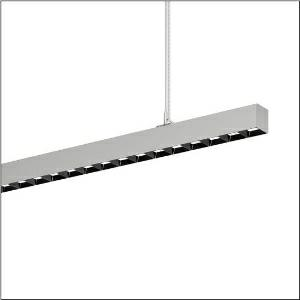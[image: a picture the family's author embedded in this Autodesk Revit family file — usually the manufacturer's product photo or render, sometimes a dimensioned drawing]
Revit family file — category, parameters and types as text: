
# Revit family: silica_r__21_51mx32tctds_853f
name_source: partatom
category: Lighting Fixtures
units: mm (PartAtom-declared; Revit-internal decimal feet)

## family parameters
Cut with Voids When Loaded = No
Host = Face
Light Source = No
Part Type = Normal
Room Calculation Point = No
Round Connector Dimension = Use Diameter
Shared = No

## types (1)
- --- (1 x LED, 15540 lm, 133.6 W, 6500K)
    Apparent Load = 134 VA
    CIE Flux Codes = 84 99 100 60 100
    Color Rendering = 80
    Color Temperature = 6500K
    Default Elevation = 1800 mm
    Description = Silica® 21, office luminaire, primary light control with darklight reflector, of PMMA, black, CAT 2 (L<= 3000cd/m²), light emission: direct/indirect distribution, primary light characteristic: symmetric, installation type: suspended mounting, LED, rated luminous flux: 15.540lm, luminous efficacy: 111lm/W, light colour: 8tw, colour temperature: 2700..6500K, control gear: ECG DALI, with terminal, 3+2-pole, max. 2.5mm², mains connection: 220..240V, AC, 50/60Hz, rated input power: 140.3W, luminaire housing, of aluminium, metallic grey (RAL 9006), length: 3.004mm, width: 53mm, height: 53mm, protection rating (complete): IP20, insulation class (complete): insulation class I (protective earthing), certification: CE, permissible operating ambient temperature: 0..+35°C, standard: EN 50419, packaging unit: 1 piece
    Height = 53 mm
    Lamp = 1 x LED
    Lamp Light Flux = 15540 lm
    Lamp Power = 133.6 W
    Lamp count = 1
    Length = 3004 mm
    Luminous efficacy = 116 lm/W
    Manufacturer = Siteco
    ModVariant = No
    Model = 51MX32TCTDS
    Mounting Place = Ceiling
    Mounting Type = Pendant
    Number of Poles = 1
    OnlyDefault = Yes
    Power Factor = 1
    Product Name = Silica® 21
    Product group = office luminaire | ceiling pendant
    ProductGroupID = 905
    Protection Class = Protection class I
    Protection Degree = IP 20
    RLX_Detail_Level = 1
    RlxData = <blob elided: 61785 chars, md5=ebc5dc4c>
    Socket = socket
    Standby Power = 0 W
    System Light Flux = 15540 lm
    System Power = 134 W
    Type Comments = individual setting
    Type Image = l_1251731.jpg
    URL = http://relux.com
    VarID = @adj_046005
    Voltage = 0 V
    Weight = 0.00 kg
    Width = 53 mm

## geometry (parser evidence)
native form markers: Blend x4, Sweep x15
no freeform markers — native parametric forms only
